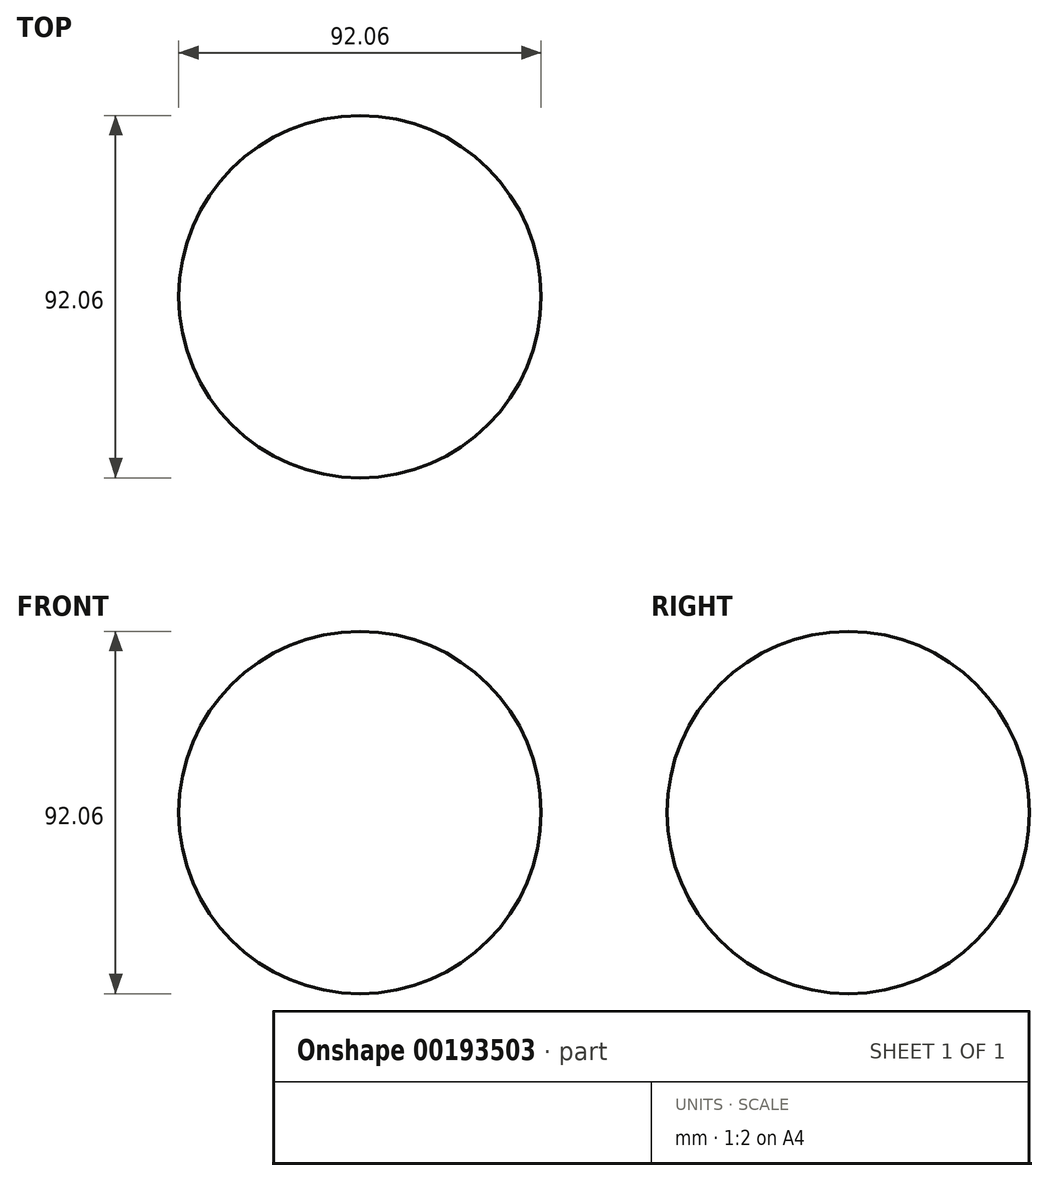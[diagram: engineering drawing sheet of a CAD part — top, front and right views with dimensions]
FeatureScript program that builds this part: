
annotation { "Feature Type Name" : "Feature", "Feature Type Description" : "" }
export const myFeature = defineFeature(function(context is Context, id is Id, definition is map)
    precondition{}
    {
        {
            var Q0;
            Q0=qCreatedBy(makeId("Front.planeOp"),FACE);
            var sketch = newSketch(context, id + "F0", { "sketchPlane" : qUnion([Q0])});
            skArc(sketch, "E0", {"start": v(46.03, 0) * mm, "mid": v(0, 46.03) * mm, "end": v(-46.03, 0) * mm});
            skLineSegment(sketch, "E1", {"start": v(-46.03, 0) * mm, "end": v(46.03, 0) * mm});
            skSolve(sketch);
        }
        {
            var Q0;
            Q0=makeQuery(id+"F0.imprint","IMPRINT",FACE,{"disambiguationData":[TD([[makeQuery(id+"F0.imprint","IMPRINT",EDGE,{"derivedFrom":sQuery(id+"F0.wireOp",EDGE,"E0")}),1.0]])]});
            var Q1;
            Q1=sQuery(id+"F0.wireOp",EDGE,"E1");
            revolve(context, id + "F1", {"entities" : qUnion([Q0]), "axis" : qUnion([Q1]), "revolveType" : RevolveType.FULL});
        }
    });
